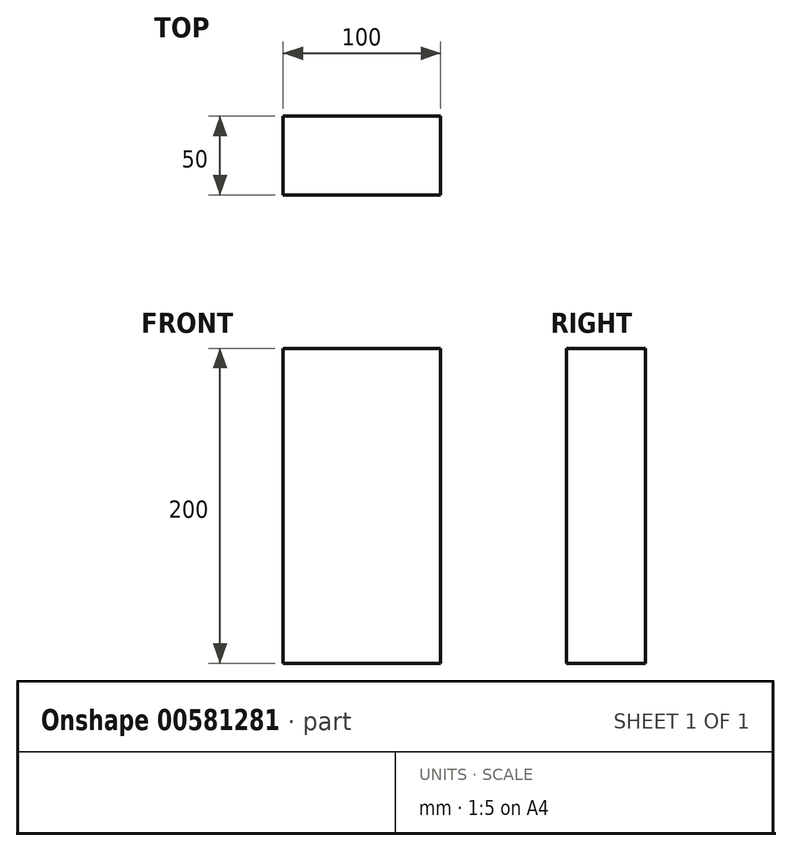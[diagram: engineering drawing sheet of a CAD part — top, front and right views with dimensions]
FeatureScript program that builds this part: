
annotation { "Feature Type Name" : "Feature", "Feature Type Description" : "" }
export const myFeature = defineFeature(function(context is Context, id is Id, definition is map)
    precondition{}
    {
        {
            var Q0;
            Q0=qCreatedBy(makeId("Front.planeOp"),FACE);
            var sketch = newSketch(context, id + "F0", { "sketchPlane" : qUnion([Q0])});
            skLineSegment(sketch, "E0.bottom", {"start": v(50, 0) * mm, "end": v(-50, 0) * mm});
            skLineSegment(sketch, "E0.top", {"start": v(50, -200) * mm, "end": v(-50, -200) * mm});
            skLineSegment(sketch, "E0.left", {"start": v(50, 0) * mm, "end": v(50, -200) * mm});
            skLineSegment(sketch, "E0.right", {"start": v(-50, 0) * mm, "end": v(-50, -200) * mm});
            skSolve(sketch);
        }
        {
            var Q0;
            Q0=makeQuery(id+"F0.imprint","IMPRINT",FACE,{"disambiguationData":[TD([[makeQuery(id+"F0.imprint","IMPRINT",EDGE,{"derivedFrom":sQuery(id+"F0.wireOp",EDGE,"E0.bottom")}),1.0]])]});
            extrude(context, id + "F1", {"entities" : qUnion([Q0]), "depth" : 50 * mm, "offsetDistance" : 25 * mm});
        }
    });
